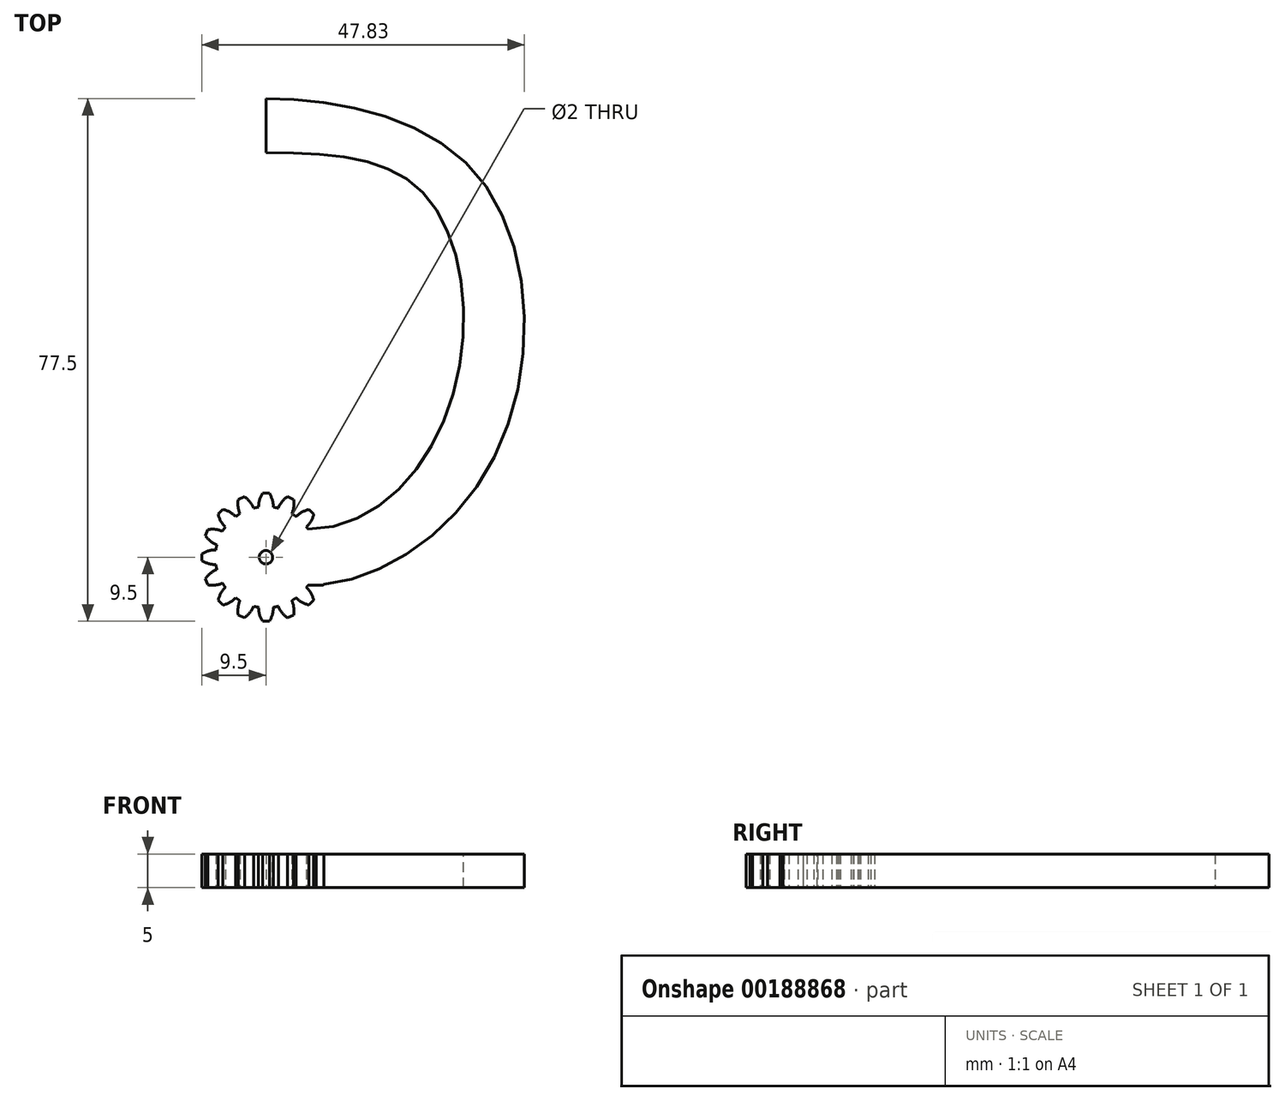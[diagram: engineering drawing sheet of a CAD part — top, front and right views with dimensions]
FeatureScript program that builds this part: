
annotation { "Feature Type Name" : "Feature", "Feature Type Description" : "" }
export const myFeature = defineFeature(function(context is Context, id is Id, definition is map)
    precondition{}
    {
        {
            var Q0;
            Q0=qCreatedBy(makeId("Top.planeOp"),FACE);
            var sketch = newSketch(context, id + "F0", { "sketchPlane" : qUnion([Q0])});
            skCircle(sketch, "E0", {"center": v(0, 0) * mm, "radius": 7.5 * mm});
            skLineSegment(sketch, "E1", {"start": v(0, 0) * mm, "end": v(0, 7.5) * mm, "construction": true});
            skLineSegment(sketch, "E2", {"start": v(0, 9.5) * mm, "end": v(-0.5, 9.5) * mm});
            skArc(sketch, "E3", {"start": v(-0.5, 9.5) * mm, "mid": v(-0.95, 8.5) * mm, "end": v(-1.09, 7.42) * mm});
            skLineSegment(sketch, "E4.MirrorCS", {"start": v(0, 9.5) * mm, "end": v(0.5, 9.5) * mm});
            skArc(sketch, "E5.MirrorCS", {"start": v(0.5, 9.5) * mm, "mid": v(0.95, 8.5) * mm, "end": v(1.09, 7.42) * mm});
            skArc(sketch, "E6.1.0", {"start": v(-4.1, 8.59) * mm, "mid": v(-4.13, 7.5) * mm, "end": v(-3.85, 6.44) * mm});
            skLineSegment(sketch, "E6.1.1", {"start": v(-3.64, 8.78) * mm, "end": v(-4.1, 8.59) * mm});
            skLineSegment(sketch, "E6.1.2", {"start": v(-3.64, 8.78) * mm, "end": v(-3.17, 8.97) * mm});
            skArc(sketch, "E6.1.3", {"start": v(-3.17, 8.97) * mm, "mid": v(-2.38, 8.22) * mm, "end": v(-1.83, 7.27) * mm});
            skArc(sketch, "E6.2.0", {"start": v(-7.07, 6.36) * mm, "mid": v(-6.69, 5.34) * mm, "end": v(-6.02, 4.48) * mm});
            skLineSegment(sketch, "E6.2.1", {"start": v(-6.72, 6.72) * mm, "end": v(-7.07, 6.36) * mm});
            skLineSegment(sketch, "E6.2.2", {"start": v(-6.72, 6.72) * mm, "end": v(-6.36, 7.07) * mm});
            skArc(sketch, "E6.2.3", {"start": v(-6.36, 7.07) * mm, "mid": v(-5.34, 6.69) * mm, "end": v(-4.48, 6.02) * mm});
            skArc(sketch, "E6.3.0", {"start": v(-8.97, 3.17) * mm, "mid": v(-8.22, 2.38) * mm, "end": v(-7.27, 1.83) * mm});
            skLineSegment(sketch, "E6.3.1", {"start": v(-8.78, 3.64) * mm, "end": v(-8.97, 3.17) * mm});
            skLineSegment(sketch, "E6.3.2", {"start": v(-8.78, 3.64) * mm, "end": v(-8.59, 4.1) * mm});
            skArc(sketch, "E6.3.3", {"start": v(-8.59, 4.1) * mm, "mid": v(-7.5, 4.13) * mm, "end": v(-6.44, 3.85) * mm});
            skArc(sketch, "E6.4.0", {"start": v(-9.5, -0.5) * mm, "mid": v(-8.5, -0.95) * mm, "end": v(-7.42, -1.09) * mm});
            skLineSegment(sketch, "E6.4.1", {"start": v(-9.5, 0) * mm, "end": v(-9.5, -0.5) * mm});
            skLineSegment(sketch, "E6.4.2", {"start": v(-9.5, 0) * mm, "end": v(-9.5, 0.5) * mm});
            skArc(sketch, "E6.4.3", {"start": v(-9.5, 0.5) * mm, "mid": v(-8.5, 0.95) * mm, "end": v(-7.42, 1.09) * mm});
            skArc(sketch, "E6.5.0", {"start": v(-8.59, -4.1) * mm, "mid": v(-7.5, -4.13) * mm, "end": v(-6.44, -3.85) * mm});
            skLineSegment(sketch, "E6.5.1", {"start": v(-8.78, -3.64) * mm, "end": v(-8.59, -4.1) * mm});
            skLineSegment(sketch, "E6.5.2", {"start": v(-8.78, -3.64) * mm, "end": v(-8.97, -3.17) * mm});
            skArc(sketch, "E6.5.3", {"start": v(-8.97, -3.17) * mm, "mid": v(-8.22, -2.38) * mm, "end": v(-7.27, -1.83) * mm});
            skArc(sketch, "E6.6.0", {"start": v(-6.36, -7.07) * mm, "mid": v(-5.34, -6.69) * mm, "end": v(-4.48, -6.02) * mm});
            skLineSegment(sketch, "E6.6.1", {"start": v(-6.72, -6.72) * mm, "end": v(-6.36, -7.07) * mm});
            skLineSegment(sketch, "E6.6.2", {"start": v(-6.72, -6.72) * mm, "end": v(-7.07, -6.36) * mm});
            skArc(sketch, "E6.6.3", {"start": v(-7.07, -6.36) * mm, "mid": v(-6.69, -5.34) * mm, "end": v(-6.02, -4.48) * mm});
            skArc(sketch, "E6.7.0", {"start": v(-3.17, -8.97) * mm, "mid": v(-2.38, -8.22) * mm, "end": v(-1.83, -7.27) * mm});
            skLineSegment(sketch, "E6.7.1", {"start": v(-3.64, -8.78) * mm, "end": v(-3.17, -8.97) * mm});
            skLineSegment(sketch, "E6.7.2", {"start": v(-3.64, -8.78) * mm, "end": v(-4.1, -8.59) * mm});
            skArc(sketch, "E6.7.3", {"start": v(-4.1, -8.59) * mm, "mid": v(-4.13, -7.5) * mm, "end": v(-3.85, -6.44) * mm});
            skArc(sketch, "E6.8.0", {"start": v(0.5, -9.5) * mm, "mid": v(0.95, -8.5) * mm, "end": v(1.09, -7.42) * mm});
            skLineSegment(sketch, "E6.8.1", {"start": v(0, -9.5) * mm, "end": v(0.5, -9.5) * mm});
            skLineSegment(sketch, "E6.8.2", {"start": v(0, -9.5) * mm, "end": v(-0.5, -9.5) * mm});
            skArc(sketch, "E6.8.3", {"start": v(-0.5, -9.5) * mm, "mid": v(-0.95, -8.5) * mm, "end": v(-1.09, -7.42) * mm});
            skArc(sketch, "E6.9.0", {"start": v(4.1, -8.59) * mm, "mid": v(4.13, -7.5) * mm, "end": v(3.85, -6.44) * mm});
            skLineSegment(sketch, "E6.9.1", {"start": v(3.64, -8.78) * mm, "end": v(4.1, -8.59) * mm});
            skLineSegment(sketch, "E6.9.2", {"start": v(3.64, -8.78) * mm, "end": v(3.17, -8.97) * mm});
            skArc(sketch, "E6.9.3", {"start": v(3.17, -8.97) * mm, "mid": v(2.38, -8.22) * mm, "end": v(1.83, -7.27) * mm});
            skArc(sketch, "E6.10.0", {"start": v(7.07, -6.36) * mm, "mid": v(6.69, -5.34) * mm, "end": v(6.02, -4.48) * mm});
            skLineSegment(sketch, "E6.10.1", {"start": v(6.72, -6.72) * mm, "end": v(7.07, -6.36) * mm});
            skLineSegment(sketch, "E6.10.2", {"start": v(6.72, -6.72) * mm, "end": v(6.36, -7.07) * mm});
            skArc(sketch, "E6.10.3", {"start": v(6.36, -7.07) * mm, "mid": v(5.34, -6.69) * mm, "end": v(4.48, -6.02) * mm});
            skArc(sketch, "E6.11.0", {"start": v(8.97, -3.17) * mm, "mid": v(8.22, -2.38) * mm, "end": v(7.27, -1.83) * mm});
            skLineSegment(sketch, "E6.11.1", {"start": v(8.78, -3.64) * mm, "end": v(8.97, -3.17) * mm});
            skLineSegment(sketch, "E6.11.2", {"start": v(8.78, -3.64) * mm, "end": v(8.59, -4.1) * mm});
            skArc(sketch, "E6.11.3", {"start": v(8.59, -4.1) * mm, "mid": v(7.5, -4.13) * mm, "end": v(6.44, -3.85) * mm});
            skArc(sketch, "E6.12.0", {"start": v(9.5, 0.5) * mm, "mid": v(8.5, 0.95) * mm, "end": v(7.42, 1.09) * mm});
            skLineSegment(sketch, "E6.12.1", {"start": v(9.5, 0) * mm, "end": v(9.5, 0.5) * mm});
            skLineSegment(sketch, "E6.12.2", {"start": v(9.5, 0) * mm, "end": v(9.5, -0.5) * mm});
            skArc(sketch, "E6.12.3", {"start": v(9.5, -0.5) * mm, "mid": v(8.5, -0.95) * mm, "end": v(7.42, -1.09) * mm});
            skArc(sketch, "E6.13.0", {"start": v(8.59, 4.1) * mm, "mid": v(7.5, 4.13) * mm, "end": v(6.44, 3.85) * mm});
            skLineSegment(sketch, "E6.13.1", {"start": v(8.78, 3.64) * mm, "end": v(8.59, 4.1) * mm});
            skLineSegment(sketch, "E6.13.2", {"start": v(8.78, 3.64) * mm, "end": v(8.97, 3.17) * mm});
            skArc(sketch, "E6.13.3", {"start": v(8.97, 3.17) * mm, "mid": v(8.22, 2.38) * mm, "end": v(7.27, 1.83) * mm});
            skArc(sketch, "E6.14.0", {"start": v(6.36, 7.07) * mm, "mid": v(5.34, 6.69) * mm, "end": v(4.48, 6.02) * mm});
            skLineSegment(sketch, "E6.14.1", {"start": v(6.72, 6.72) * mm, "end": v(6.36, 7.07) * mm});
            skLineSegment(sketch, "E6.14.2", {"start": v(6.72, 6.72) * mm, "end": v(7.07, 6.36) * mm});
            skArc(sketch, "E6.14.3", {"start": v(7.07, 6.36) * mm, "mid": v(6.69, 5.34) * mm, "end": v(6.02, 4.48) * mm});
            skArc(sketch, "E6.15.0", {"start": v(3.17, 8.97) * mm, "mid": v(2.38, 8.22) * mm, "end": v(1.83, 7.27) * mm});
            skLineSegment(sketch, "E6.15.1", {"start": v(3.64, 8.78) * mm, "end": v(3.17, 8.97) * mm});
            skLineSegment(sketch, "E6.15.2", {"start": v(3.64, 8.78) * mm, "end": v(4.1, 8.59) * mm});
            skArc(sketch, "E6.15.3", {"start": v(4.1, 8.59) * mm, "mid": v(4.13, 7.5) * mm, "end": v(3.85, 6.44) * mm});
            skSolve(sketch);
        }
        {
            var Q0;
            Q0=qSketchRegion(id+"F0",true);
            extrude(context, id + "F1", {"entities" : qUnion([Q0]), "depth" : 5 * mm});
        }
        {
            var Q0;
            Q0=makeQuery(id+"F1.opExtrude","CAP_FACE",FACE,{"disambiguationData":[OSD([sQuery(id+"F0.wireOp",EDGE,"E0"),sQuery(id+"F0.wireOp",EDGE,"E2"),sQuery(id+"F0.wireOp",EDGE,"E3"),sQuery(id+"F0.wireOp",EDGE,"E4.MirrorCS"),sQuery(id+"F0.wireOp",EDGE,"E5.MirrorCS"),sQuery(id+"F0.wireOp",EDGE,"E6.1.0"),sQuery(id+"F0.wireOp",EDGE,"E6.1.1"),sQuery(id+"F0.wireOp",EDGE,"E6.1.2"),sQuery(id+"F0.wireOp",EDGE,"E6.1.3"),sQuery(id+"F0.wireOp",EDGE,"E6.2.0"),sQuery(id+"F0.wireOp",EDGE,"E6.2.1"),sQuery(id+"F0.wireOp",EDGE,"E6.2.2"),sQuery(id+"F0.wireOp",EDGE,"E6.2.3"),sQuery(id+"F0.wireOp",EDGE,"E6.3.0"),sQuery(id+"F0.wireOp",EDGE,"E6.3.1"),sQuery(id+"F0.wireOp",EDGE,"E6.3.2"),sQuery(id+"F0.wireOp",EDGE,"E6.3.3"),sQuery(id+"F0.wireOp",EDGE,"E6.4.0"),sQuery(id+"F0.wireOp",EDGE,"E6.4.1"),sQuery(id+"F0.wireOp",EDGE,"E6.4.2"),sQuery(id+"F0.wireOp",EDGE,"E6.4.3"),sQuery(id+"F0.wireOp",EDGE,"E6.5.0"),sQuery(id+"F0.wireOp",EDGE,"E6.5.1"),sQuery(id+"F0.wireOp",EDGE,"E6.5.2"),sQuery(id+"F0.wireOp",EDGE,"E6.5.3"),sQuery(id+"F0.wireOp",EDGE,"E6.6.0"),sQuery(id+"F0.wireOp",EDGE,"E6.6.1"),sQuery(id+"F0.wireOp",EDGE,"E6.6.2"),sQuery(id+"F0.wireOp",EDGE,"E6.6.3"),sQuery(id+"F0.wireOp",EDGE,"E6.7.0"),sQuery(id+"F0.wireOp",EDGE,"E6.7.1"),sQuery(id+"F0.wireOp",EDGE,"E6.7.2"),sQuery(id+"F0.wireOp",EDGE,"E6.7.3"),sQuery(id+"F0.wireOp",EDGE,"E6.8.0"),sQuery(id+"F0.wireOp",EDGE,"E6.8.1"),sQuery(id+"F0.wireOp",EDGE,"E6.8.2"),sQuery(id+"F0.wireOp",EDGE,"E6.8.3"),sQuery(id+"F0.wireOp",EDGE,"E6.9.0"),sQuery(id+"F0.wireOp",EDGE,"E6.9.1"),sQuery(id+"F0.wireOp",EDGE,"E6.9.2"),sQuery(id+"F0.wireOp",EDGE,"E6.9.3"),sQuery(id+"F0.wireOp",EDGE,"E6.10.0"),sQuery(id+"F0.wireOp",EDGE,"E6.10.1"),sQuery(id+"F0.wireOp",EDGE,"E6.10.2"),sQuery(id+"F0.wireOp",EDGE,"E6.10.3"),sQuery(id+"F0.wireOp",EDGE,"E6.11.0"),sQuery(id+"F0.wireOp",EDGE,"E6.11.1"),sQuery(id+"F0.wireOp",EDGE,"E6.11.2"),sQuery(id+"F0.wireOp",EDGE,"E6.11.3"),sQuery(id+"F0.wireOp",EDGE,"E6.12.0"),sQuery(id+"F0.wireOp",EDGE,"E6.12.1"),sQuery(id+"F0.wireOp",EDGE,"E6.12.2"),sQuery(id+"F0.wireOp",EDGE,"E6.12.3"),sQuery(id+"F0.wireOp",EDGE,"E6.13.0"),sQuery(id+"F0.wireOp",EDGE,"E6.13.1"),sQuery(id+"F0.wireOp",EDGE,"E6.13.2"),sQuery(id+"F0.wireOp",EDGE,"E6.13.3"),sQuery(id+"F0.wireOp",EDGE,"E6.14.0"),sQuery(id+"F0.wireOp",EDGE,"E6.14.1"),sQuery(id+"F0.wireOp",EDGE,"E6.14.2"),sQuery(id+"F0.wireOp",EDGE,"E6.14.3"),sQuery(id+"F0.wireOp",EDGE,"E6.15.0"),sQuery(id+"F0.wireOp",EDGE,"E6.15.1"),sQuery(id+"F0.wireOp",EDGE,"E6.15.2"),sQuery(id+"F0.wireOp",EDGE,"E6.15.3")])],"isStart":false});
            var sketch = newSketch(context, id + "F2", { "sketchPlane" : qUnion([Q0])});
            skCircle(sketch, "E7", {"center": v(0, 0) * mm, "radius": 1 * mm});
            skSolve(sketch);
        }
        {
            var Q0;
            Q0=qSketchRegion(id+"F2",true);
            extrude(context, id + "F3", {"entities" : qUnion([Q0]), "operationType" : NewBodyOperationType.REMOVE, "endBound" : BoundingType.THROUGH_ALL, "oppositeDirection" : true, "depth" : 25 * mm});
        }
        {
            var Q0;
            Q0=qCreatedBy(makeId("Top.planeOp"),FACE);
            var sketch = newSketch(context, id + "F4", { "sketchPlane" : qUnion([Q0])});
            skLineSegment(sketch, "E8", {"start": v(0, 68) * mm, "end": v(0, 60) * mm});
            skFitSpline(sketch, "E9", {"points": [v(0, 60) * mm, v(23.7, 53.63) * mm, v(27.5, 23.3) * mm, v(6.24, 4.17) * mm], "startDerivative": vector(95.87, 0) * mm, "endDerivative": vector(-88.79, 0) * mm});
            skFitSpline(sketch, "E10", {"points": [v(0, 68) * mm, v(31.4, 56.6) * mm, v(33.82, 14.72) * mm, v(6.24, -4.17) * mm], "startDerivative": vector(93.63, 0) * mm, "endDerivative": vector(-93.59, 0) * mm});
            skLineSegment(sketch, "E11", {"start": v(6.24, 4.17) * mm, "end": v(6.24, -4.17) * mm});
            skSolve(sketch);
        }
        {
            var Q0;
            Q0=qSketchRegion(id+"F4",true);
            var Q1;
            Q1=makeQuery(id+"F1.opExtrude","CAP_FACE",FACE,{"disambiguationData":[OSD([sQuery(id+"F0.wireOp",EDGE,"E0"),sQuery(id+"F0.wireOp",EDGE,"E2"),sQuery(id+"F0.wireOp",EDGE,"E3"),sQuery(id+"F0.wireOp",EDGE,"E4.MirrorCS"),sQuery(id+"F0.wireOp",EDGE,"E5.MirrorCS"),sQuery(id+"F0.wireOp",EDGE,"E6.1.0"),sQuery(id+"F0.wireOp",EDGE,"E6.1.1"),sQuery(id+"F0.wireOp",EDGE,"E6.1.2"),sQuery(id+"F0.wireOp",EDGE,"E6.1.3"),sQuery(id+"F0.wireOp",EDGE,"E6.2.0"),sQuery(id+"F0.wireOp",EDGE,"E6.2.1"),sQuery(id+"F0.wireOp",EDGE,"E6.2.2"),sQuery(id+"F0.wireOp",EDGE,"E6.2.3"),sQuery(id+"F0.wireOp",EDGE,"E6.3.0"),sQuery(id+"F0.wireOp",EDGE,"E6.3.1"),sQuery(id+"F0.wireOp",EDGE,"E6.3.2"),sQuery(id+"F0.wireOp",EDGE,"E6.3.3"),sQuery(id+"F0.wireOp",EDGE,"E6.4.0"),sQuery(id+"F0.wireOp",EDGE,"E6.4.1"),sQuery(id+"F0.wireOp",EDGE,"E6.4.2"),sQuery(id+"F0.wireOp",EDGE,"E6.4.3"),sQuery(id+"F0.wireOp",EDGE,"E6.5.0"),sQuery(id+"F0.wireOp",EDGE,"E6.5.1"),sQuery(id+"F0.wireOp",EDGE,"E6.5.2"),sQuery(id+"F0.wireOp",EDGE,"E6.5.3"),sQuery(id+"F0.wireOp",EDGE,"E6.6.0"),sQuery(id+"F0.wireOp",EDGE,"E6.6.1"),sQuery(id+"F0.wireOp",EDGE,"E6.6.2"),sQuery(id+"F0.wireOp",EDGE,"E6.6.3"),sQuery(id+"F0.wireOp",EDGE,"E6.7.0"),sQuery(id+"F0.wireOp",EDGE,"E6.7.1"),sQuery(id+"F0.wireOp",EDGE,"E6.7.2"),sQuery(id+"F0.wireOp",EDGE,"E6.7.3"),sQuery(id+"F0.wireOp",EDGE,"E6.8.0"),sQuery(id+"F0.wireOp",EDGE,"E6.8.1"),sQuery(id+"F0.wireOp",EDGE,"E6.8.2"),sQuery(id+"F0.wireOp",EDGE,"E6.8.3"),sQuery(id+"F0.wireOp",EDGE,"E6.9.0"),sQuery(id+"F0.wireOp",EDGE,"E6.9.1"),sQuery(id+"F0.wireOp",EDGE,"E6.9.2"),sQuery(id+"F0.wireOp",EDGE,"E6.9.3"),sQuery(id+"F0.wireOp",EDGE,"E6.10.0"),sQuery(id+"F0.wireOp",EDGE,"E6.10.1"),sQuery(id+"F0.wireOp",EDGE,"E6.10.2"),sQuery(id+"F0.wireOp",EDGE,"E6.10.3"),sQuery(id+"F0.wireOp",EDGE,"E6.11.0"),sQuery(id+"F0.wireOp",EDGE,"E6.11.1"),sQuery(id+"F0.wireOp",EDGE,"E6.11.2"),sQuery(id+"F0.wireOp",EDGE,"E6.11.3"),sQuery(id+"F0.wireOp",EDGE,"E6.12.0"),sQuery(id+"F0.wireOp",EDGE,"E6.12.1"),sQuery(id+"F0.wireOp",EDGE,"E6.12.2"),sQuery(id+"F0.wireOp",EDGE,"E6.12.3"),sQuery(id+"F0.wireOp",EDGE,"E6.13.0"),sQuery(id+"F0.wireOp",EDGE,"E6.13.1"),sQuery(id+"F0.wireOp",EDGE,"E6.13.2"),sQuery(id+"F0.wireOp",EDGE,"E6.13.3"),sQuery(id+"F0.wireOp",EDGE,"E6.14.0"),sQuery(id+"F0.wireOp",EDGE,"E6.14.1"),sQuery(id+"F0.wireOp",EDGE,"E6.14.2"),sQuery(id+"F0.wireOp",EDGE,"E6.14.3"),sQuery(id+"F0.wireOp",EDGE,"E6.15.0"),sQuery(id+"F0.wireOp",EDGE,"E6.15.1"),sQuery(id+"F0.wireOp",EDGE,"E6.15.2"),sQuery(id+"F0.wireOp",EDGE,"E6.15.3")])],"isStart":false});
            extrude(context, id + "F5", {"entities" : qUnion([Q0]), "operationType" : NewBodyOperationType.ADD, "endBound" : BoundingType.UP_TO_SURFACE, "endBoundEntityFace" : qUnion([Q1]), "depth" : 25 * mm});
        }
    });
